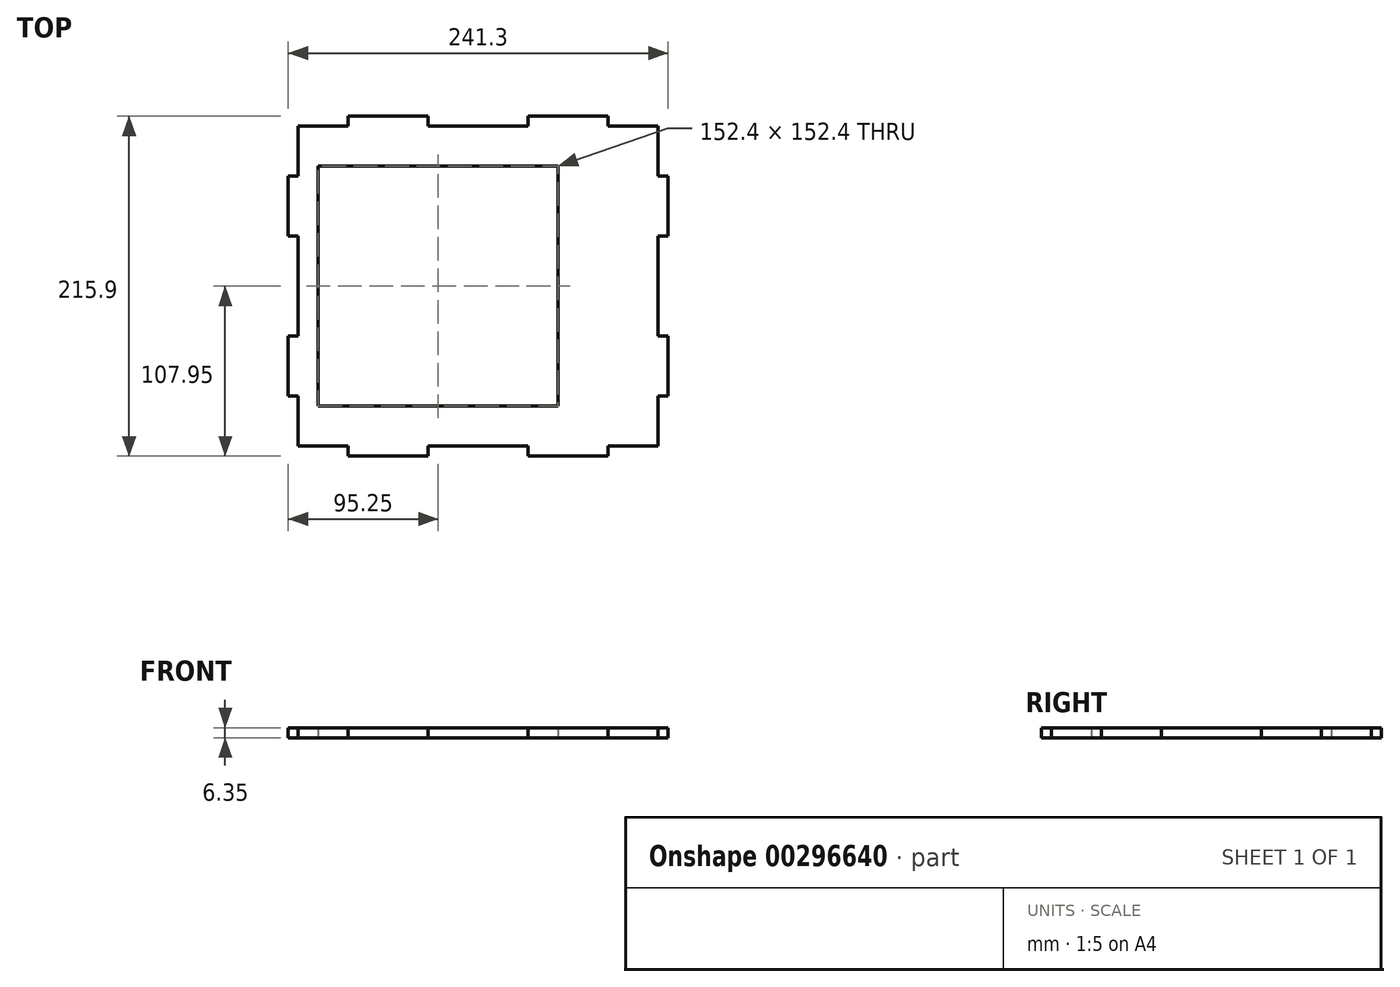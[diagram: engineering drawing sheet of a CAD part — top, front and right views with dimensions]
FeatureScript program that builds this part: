
annotation { "Feature Type Name" : "Feature", "Feature Type Description" : "" }
export const myFeature = defineFeature(function(context is Context, id is Id, definition is map)
    precondition{}
    {
        {
            var Q0;
            Q0=qCreatedBy(makeId("Top.planeOp"),FACE);
            var sketch = newSketch(context, id + "F0", { "sketchPlane" : qUnion([Q0])});
            skLineSegment(sketch, "E0.bottom", {"start": v(76.2, 76.2) * mm, "end": v(-76.2, 76.2) * mm});
            skLineSegment(sketch, "E0.top", {"start": v(76.2, -76.2) * mm, "end": v(-76.2, -76.2) * mm});
            skLineSegment(sketch, "E0.left", {"start": v(76.2, 76.2) * mm, "end": v(76.2, -76.2) * mm});
            skLineSegment(sketch, "E0.right", {"start": v(-76.2, 76.2) * mm, "end": v(-76.2, -76.2) * mm});
            skPoint(sketch, "E0.middle", {"position": v(0, 0) * mm});
            skLineSegment(sketch, "E1.bottom", {"start": v(-88.9, 101.6) * mm, "end": v(139.7, 101.6) * mm});
            skLineSegment(sketch, "E1.top", {"start": v(-88.9, -101.6) * mm, "end": v(139.7, -101.6) * mm});
            skLineSegment(sketch, "E1.left", {"start": v(-88.9, 101.6) * mm, "end": v(-88.9, -101.6) * mm});
            skLineSegment(sketch, "E1.right", {"start": v(139.7, 101.6) * mm, "end": v(139.7, -101.6) * mm});
            skPoint(sketch, "E1.middle", {"position": v(25.4, 0) * mm});
            skSolve(sketch);
        }
        {
            var Q0;
            Q0 = qSketchRegion(id + "F0", true);
            extrude(context, id + "F1", {"entities" : qUnion([Q0]), "depth" : 6.35 * mm});
        }
        {
            var Q0;
            Q0=makeQuery(id+"F1.opExtrude","CAP_FACE",FACE,{"disambiguationData":[OSD([sQuery(id+"F0.wireOp",EDGE,"E0.bottom"),sQuery(id+"F0.wireOp",EDGE,"E0.top"),sQuery(id+"F0.wireOp",EDGE,"E0.left"),sQuery(id+"F0.wireOp",EDGE,"E0.right"),sQuery(id+"F0.wireOp",EDGE,"E1.bottom"),sQuery(id+"F0.wireOp",EDGE,"E1.top"),sQuery(id+"F0.wireOp",EDGE,"E1.left"),sQuery(id+"F0.wireOp",EDGE,"E1.right")])],"isStart":false});
            var sketch = newSketch(context, id + "F2", { "sketchPlane" : qUnion([Q0])});
            skLineSegment(sketch, "E2", {"start": v(25.4, 101.6) * mm, "end": v(25.4, -101.6) * mm, "construction": true});
            skLineSegment(sketch, "E3", {"start": v(-88.9, 0) * mm, "end": v(139.7, 0) * mm, "construction": true});
            skLineSegment(sketch, "E4.bottom", {"start": v(-57.15, 101.6) * mm, "end": v(-6.35, 101.6) * mm});
            skLineSegment(sketch, "E4.top", {"start": v(-57.15, 107.95) * mm, "end": v(-6.35, 107.95) * mm});
            skLineSegment(sketch, "E4.left", {"start": v(-57.15, 101.6) * mm, "end": v(-57.15, 107.95) * mm});
            skLineSegment(sketch, "E4.right", {"start": v(-6.35, 101.6) * mm, "end": v(-6.35, 107.95) * mm});
            skLineSegment(sketch, "E5.bottom", {"start": v(57.15, 101.6) * mm, "end": v(107.95, 101.6) * mm});
            skLineSegment(sketch, "E5.top", {"start": v(57.15, 107.95) * mm, "end": v(107.95, 107.95) * mm});
            skLineSegment(sketch, "E5.left", {"start": v(57.15, 101.6) * mm, "end": v(57.15, 107.95) * mm});
            skLineSegment(sketch, "E5.right", {"start": v(107.95, 101.6) * mm, "end": v(107.95, 107.95) * mm});
            skLineSegment(sketch, "E6.bottom", {"start": v(139.7, 69.85) * mm, "end": v(146.05, 69.85) * mm});
            skLineSegment(sketch, "E6.top", {"start": v(139.7, 31.75) * mm, "end": v(146.05, 31.75) * mm});
            skLineSegment(sketch, "E6.left", {"start": v(139.7, 69.85) * mm, "end": v(139.7, 31.75) * mm});
            skLineSegment(sketch, "E6.right", {"start": v(146.05, 69.85) * mm, "end": v(146.05, 31.75) * mm});
            skLineSegment(sketch, "E7.bottom", {"start": v(139.7, -31.75) * mm, "end": v(146.05, -31.75) * mm});
            skLineSegment(sketch, "E7.top", {"start": v(139.7, -69.85) * mm, "end": v(146.05, -69.85) * mm});
            skLineSegment(sketch, "E7.left", {"start": v(139.7, -31.75) * mm, "end": v(139.7, -69.85) * mm});
            skLineSegment(sketch, "E7.right", {"start": v(146.05, -31.75) * mm, "end": v(146.05, -69.85) * mm});
            skLineSegment(sketch, "E8", {"start": v(-31.75, 107.95) * mm, "end": v(-31.75, 0) * mm, "construction": true});
            skLineSegment(sketch, "E9", {"start": v(82.55, 107.95) * mm, "end": v(82.55, 0) * mm, "construction": true});
            skLineSegment(sketch, "E10", {"start": v(146.05, 50.8) * mm, "end": v(25.4, 50.8) * mm, "construction": true});
            skLineSegment(sketch, "E11", {"start": v(146.05, -50.8) * mm, "end": v(25.4, -50.8) * mm, "construction": true});
            skLineSegment(sketch, "E12.MirrorCS", {"start": v(-88.9, -31.75) * mm, "end": v(-95.25, -31.75) * mm});
            skLineSegment(sketch, "E13.MirrorCS", {"start": v(-88.9, -69.85) * mm, "end": v(-95.25, -69.85) * mm});
            skLineSegment(sketch, "E14.MirrorCS", {"start": v(-88.9, 31.75) * mm, "end": v(-95.25, 31.75) * mm});
            skLineSegment(sketch, "E15.MirrorCS", {"start": v(-88.9, 69.85) * mm, "end": v(-95.25, 69.85) * mm});
            skLineSegment(sketch, "E16.MirrorCS", {"start": v(-88.9, 69.85) * mm, "end": v(-88.9, 31.75) * mm});
            skLineSegment(sketch, "E17.MirrorCS", {"start": v(-95.25, 50.8) * mm, "end": v(25.4, 50.8) * mm, "construction": true});
            skLineSegment(sketch, "E18.MirrorCS", {"start": v(139.7, 0) * mm, "end": v(-88.9, 0) * mm, "construction": true});
            skLineSegment(sketch, "E19.MirrorCS", {"start": v(-88.9, -31.75) * mm, "end": v(-88.9, -69.85) * mm});
            skLineSegment(sketch, "E20.MirrorCS", {"start": v(-95.25, -31.75) * mm, "end": v(-95.25, -69.85) * mm});
            skLineSegment(sketch, "E21.MirrorCS", {"start": v(-95.25, 69.85) * mm, "end": v(-95.25, 31.75) * mm});
            skLineSegment(sketch, "E22.MirrorCS", {"start": v(-95.25, -50.8) * mm, "end": v(25.4, -50.8) * mm, "construction": true});
            skLineSegment(sketch, "E23.MirrorCS", {"start": v(107.95, -101.6) * mm, "end": v(107.95, -107.95) * mm});
            skLineSegment(sketch, "E24.MirrorCS", {"start": v(57.15, -101.6) * mm, "end": v(57.15, -107.95) * mm});
            skLineSegment(sketch, "E25.MirrorCS", {"start": v(-57.15, -101.6) * mm, "end": v(-57.15, -107.95) * mm});
            skLineSegment(sketch, "E26.MirrorCS", {"start": v(-6.35, -101.6) * mm, "end": v(-6.35, -107.95) * mm});
            skLineSegment(sketch, "E27.MirrorCS", {"start": v(57.15, -101.6) * mm, "end": v(107.95, -101.6) * mm});
            skLineSegment(sketch, "E28.MirrorCS", {"start": v(57.15, -107.95) * mm, "end": v(107.95, -107.95) * mm});
            skLineSegment(sketch, "E29.MirrorCS", {"start": v(-57.15, -101.6) * mm, "end": v(-6.35, -101.6) * mm});
            skLineSegment(sketch, "E30.MirrorCS", {"start": v(-57.15, -107.95) * mm, "end": v(-6.35, -107.95) * mm});
            skSolve(sketch);
        }
        {
            var Q0;
            Q0 = qSketchRegion(id + "F2", true);
            extrude(context, id + "F3", {"entities" : qUnion([Q0]), "operationType" : NewBodyOperationType.ADD, "oppositeDirection" : true, "depth" : 6.35 * mm});
        }
    });
